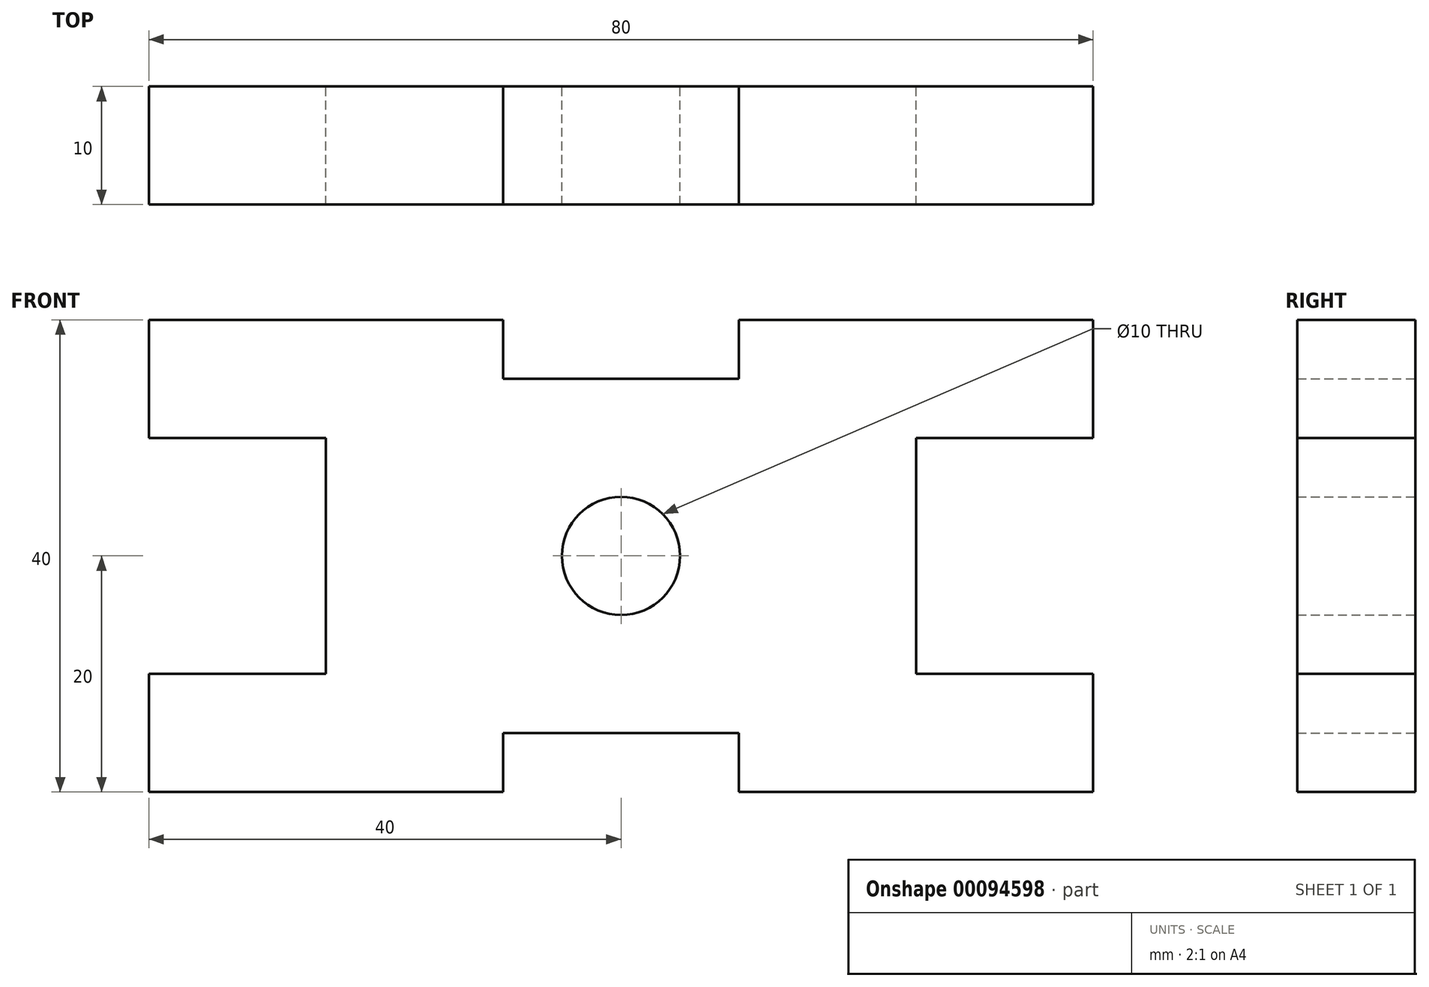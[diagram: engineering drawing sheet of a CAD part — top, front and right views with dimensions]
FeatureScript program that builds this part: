
annotation { "Feature Type Name" : "Feature", "Feature Type Description" : "" }
export const myFeature = defineFeature(function(context is Context, id is Id, definition is map)
    precondition{}
    {
        {
            var Q0;
            Q0=qCreatedBy(makeId("Front.planeOp"),FACE);
            var sketch = newSketch(context, id + "F0", { "sketchPlane" : qUnion([Q0])});
            skLineSegment(sketch, "E0", {"start": v(0, 0) * mm, "end": v(30, 0) * mm});
            skLineSegment(sketch, "E1", {"start": v(30, 0) * mm, "end": v(30, 5) * mm});
            skLineSegment(sketch, "E2", {"start": v(30, 5) * mm, "end": v(50, 5) * mm});
            skLineSegment(sketch, "E3", {"start": v(50, 5) * mm, "end": v(50, 0) * mm});
            skLineSegment(sketch, "E4", {"start": v(50, 0) * mm, "end": v(80, 0) * mm});
            skLineSegment(sketch, "E5", {"start": v(80, 0) * mm, "end": v(80, 10) * mm});
            skLineSegment(sketch, "E6", {"start": v(80, 10) * mm, "end": v(65, 10) * mm});
            skLineSegment(sketch, "E7", {"start": v(65, 10) * mm, "end": v(65, 30) * mm});
            skLineSegment(sketch, "E8", {"start": v(80, 30) * mm, "end": v(80, 40) * mm});
            skLineSegment(sketch, "E9", {"start": v(80, 40) * mm, "end": v(50, 40) * mm});
            skLineSegment(sketch, "E10", {"start": v(50, 40) * mm, "end": v(50, 35) * mm});
            skLineSegment(sketch, "E11", {"start": v(50, 35) * mm, "end": v(30, 35) * mm});
            skLineSegment(sketch, "E12", {"start": v(30, 35) * mm, "end": v(30, 40) * mm});
            skLineSegment(sketch, "E13", {"start": v(30, 40) * mm, "end": v(0, 40) * mm});
            skLineSegment(sketch, "E14", {"start": v(0, 40) * mm, "end": v(0, 30) * mm});
            skLineSegment(sketch, "E15", {"start": v(0, 30) * mm, "end": v(15, 30) * mm});
            skLineSegment(sketch, "E16", {"start": v(15, 30) * mm, "end": v(15, 10) * mm});
            skLineSegment(sketch, "E17", {"start": v(15, 10) * mm, "end": v(0, 10) * mm});
            skLineSegment(sketch, "E18", {"start": v(0, 10) * mm, "end": v(0, 0) * mm});
            skLineSegment(sketch, "E19", {"start": v(65, 30) * mm, "end": v(80, 30) * mm});
            skPoint(sketch, "E20.endSnap0", {"position": v(40, 35) * mm});
            skLineSegment(sketch, "E21", {"start": v(65, 20) * mm, "end": v(15, 20) * mm});
            skCircle(sketch, "E22", {"center": v(40, 20) * mm, "radius": 5 * mm});
            skSolve(sketch);
        }
        {
            var Q0;
            Q0 = qSketchRegion(id + "F0", true);
            var Q1;
            {var subQ6=sQuery(id+"F0.wireOp",EDGE,"E3");Q1=makeQuery(id+"F0.imprint","IMPRINT",FACE,{"disambiguationData":[TD([[makeQuery(id+"F0.imprint","IMPRINT",EDGE,{"derivedFrom":subQ6}),1.0]])]});}
            extrude(context, id + "F1", {"entities" : qUnion([Q0, Q1]), "depth" : 10 * mm});
        }
    });
